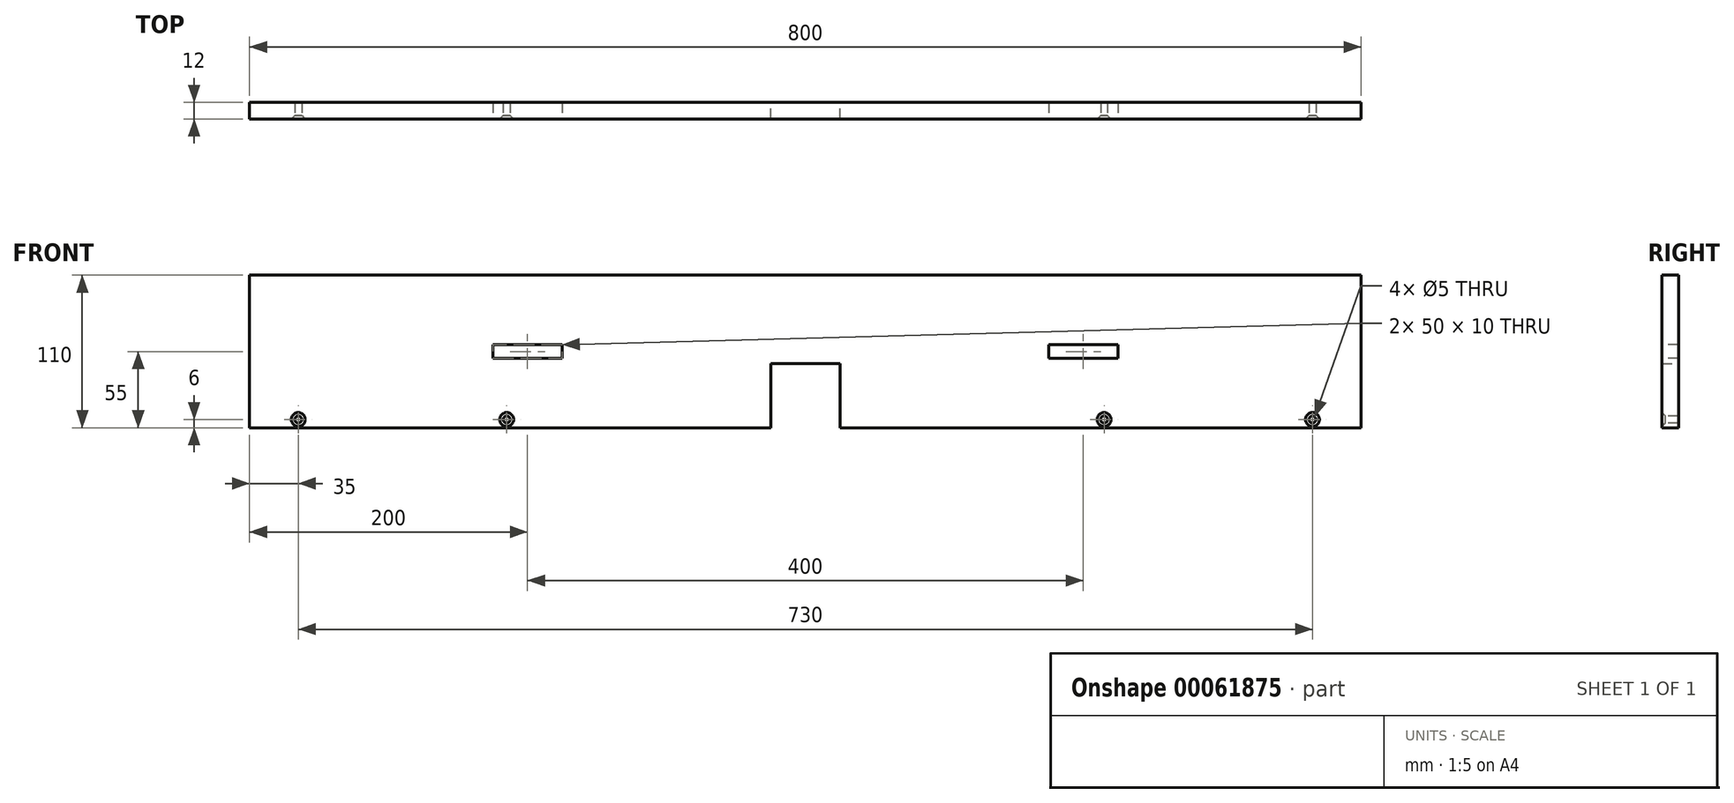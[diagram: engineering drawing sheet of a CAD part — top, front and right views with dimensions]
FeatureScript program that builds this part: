
annotation { "Feature Type Name" : "Feature", "Feature Type Description" : "" }
export const myFeature = defineFeature(function(context is Context, id is Id, definition is map)
    precondition{}
    {
        {
            var Q0;
            Q0=qCreatedBy(makeId("Front.planeOp"),FACE);
            var sketch = newSketch(context, id + "F0", { "sketchPlane" : qUnion([Q0])});
            skLineSegment(sketch, "E0.bottom", {"start": v(0, 0) * mm, "end": v(800, 0) * mm});
            skLineSegment(sketch, "E0.top", {"start": v(0, 110) * mm, "end": v(800, 110) * mm});
            skLineSegment(sketch, "E0.left", {"start": v(0, 0) * mm, "end": v(0, 110) * mm});
            skLineSegment(sketch, "E0.right", {"start": v(800, 0) * mm, "end": v(800, 110) * mm});
            skLineSegment(sketch, "E1.top", {"start": v(375, 46.26) * mm, "end": v(425, 46.26) * mm});
            skLineSegment(sketch, "E1.left", {"start": v(375, 0) * mm, "end": v(375, 46.26) * mm});
            skLineSegment(sketch, "E1.right", {"start": v(425, 0) * mm, "end": v(425, 46.26) * mm});
            skSolve(sketch);
        }
        {
            var Q0;
            Q0=makeQuery(id+"F0.imprint","IMPRINT",FACE,{"disambiguationData":[TD([[makeQuery(id+"F0.imprint","IMPRINT",EDGE,{"derivedFrom":sQuery(id+"F0.wireOp",EDGE,"E0.bottom")}),1.0]])]});
            extrude(context, id + "F1", {"entities" : qUnion([Q0]), "depth" : 12 * mm});
        }
        {
            var Q0;
            Q0=makeQuery(id+"F1.opExtrude","CAP_FACE",FACE,{"disambiguationData":[OSD([sQuery(id+"F0.wireOp",EDGE,"E0.bottom"),sQuery(id+"F0.wireOp",EDGE,"E0.top"),sQuery(id+"F0.wireOp",EDGE,"E0.left"),sQuery(id+"F0.wireOp",EDGE,"E0.right"),sQuery(id+"F0.wireOp",EDGE,"E1.top"),sQuery(id+"F0.wireOp",EDGE,"E1.left"),sQuery(id+"F0.wireOp",EDGE,"E1.right")])],"isStart":false});
            var sketch = newSketch(context, id + "F2", { "sketchPlane" : qUnion([Q0])});
            skLineSegment(sketch, "E2", {"start": v(0, 6) * mm, "end": v(800, 6) * mm, "construction": true});
            skPoint(sketch, "E3", {"position": v(35, 6) * mm});
            skPoint(sketch, "E4", {"position": v(185, 6) * mm});
            skPoint(sketch, "E5", {"position": v(615, 6) * mm});
            skPoint(sketch, "E6", {"position": v(765, 6) * mm});
            skSolve(sketch);
        }
        {
            var Q0;
            Q0=sQuery(id+"F2.wireOp",VERTEX,"E3");
            var Q1;
            Q1=sQuery(id+"F2.wireOp",VERTEX,"E4");
            var Q2;
            Q2=sQuery(id+"F2.wireOp",VERTEX,"E5");
            var Q3;
            Q3=sQuery(id+"F2.wireOp",VERTEX,"E6");
            var Q4;
            Q4=makeQuery(id+"F1.opExtrude","SWEPT_BODY",BODY,{"disambiguationData":[OSD([sQuery(id+"F0.wireOp",EDGE,"E0.bottom"),sQuery(id+"F0.wireOp",EDGE,"E0.top"),sQuery(id+"F0.wireOp",EDGE,"E0.left"),sQuery(id+"F0.wireOp",EDGE,"E0.right"),sQuery(id+"F0.wireOp",EDGE,"E1.top"),sQuery(id+"F0.wireOp",EDGE,"E1.left"),sQuery(id+"F0.wireOp",EDGE,"E1.right")])]});
            hole(context, id + "F3", {"style" : HoleStyle.C_SINK, "holeDiameter" : 5 * mm, "cSinkDiameter" : 10 * mm, "endStyle" : HoleEndStyle.THROUGH, "locations" : qUnion([Q0, Q1, Q2, Q3]), "scope" : qUnion([Q4]), "cSinkAngle" : 90 * degree});
        }
        {
            var Q0;
            Q0=makeQuery(id+"F1.opExtrude","CAP_FACE",FACE,{"disambiguationData":[OSD([sQuery(id+"F0.wireOp",EDGE,"E0.bottom"),sQuery(id+"F0.wireOp",EDGE,"E0.top"),sQuery(id+"F0.wireOp",EDGE,"E0.left"),sQuery(id+"F0.wireOp",EDGE,"E0.right"),sQuery(id+"F0.wireOp",EDGE,"E1.top"),sQuery(id+"F0.wireOp",EDGE,"E1.left"),sQuery(id+"F0.wireOp",EDGE,"E1.right")])],"isStart":false});
            var sketch = newSketch(context, id + "F4", { "sketchPlane" : qUnion([Q0])});
            skLineSegment(sketch, "E7", {"start": v(400, 110) * mm, "end": v(400, 46.26) * mm, "construction": true});
            skLineSegment(sketch, "E8", {"start": v(0, 55) * mm, "end": v(400, 55) * mm, "construction": true});
            skLineSegment(sketch, "E9", {"start": v(400, 55) * mm, "end": v(800, 55) * mm, "construction": true});
            skPoint(sketch, "E10", {"position": v(200, 55) * mm});
            skPoint(sketch, "E11", {"position": v(600, 55) * mm});
            skLineSegment(sketch, "E12.bottom", {"start": v(175, 60) * mm, "end": v(225, 60) * mm});
            skLineSegment(sketch, "E12.top", {"start": v(175, 50) * mm, "end": v(225, 50) * mm});
            skLineSegment(sketch, "E12.left", {"start": v(175, 60) * mm, "end": v(175, 50) * mm});
            skLineSegment(sketch, "E12.right", {"start": v(225, 60) * mm, "end": v(225, 50) * mm});
            skLineSegment(sketch, "E13.bottom", {"start": v(575, 60) * mm, "end": v(625, 60) * mm});
            skLineSegment(sketch, "E13.top", {"start": v(575, 50) * mm, "end": v(625, 50) * mm});
            skLineSegment(sketch, "E13.left", {"start": v(575, 60) * mm, "end": v(575, 50) * mm});
            skLineSegment(sketch, "E13.right", {"start": v(625, 60) * mm, "end": v(625, 50) * mm});
            skSolve(sketch);
        }
        {
            var Q0;
            Q0=makeQuery(id+"F4.imprint","IMPRINT",FACE,{"disambiguationData":[TD([[makeQuery(id+"F4.imprint","IMPRINT",EDGE,{"derivedFrom":sQuery(id+"F4.wireOp",EDGE,"E12.bottom")}),-1.0]])]});
            var Q1;
            Q1=makeQuery(id+"F4.imprint","IMPRINT",FACE,{"disambiguationData":[TD([[makeQuery(id+"F4.imprint","IMPRINT",EDGE,{"derivedFrom":sQuery(id+"F4.wireOp",EDGE,"E13.bottom")}),-1.0]])]});
            extrude(context, id + "F5", {"entities" : qUnion([Q0, Q1]), "operationType" : NewBodyOperationType.REMOVE, "oppositeDirection" : true, "depth" : 25 * mm});
        }
    });
